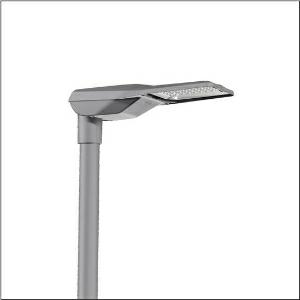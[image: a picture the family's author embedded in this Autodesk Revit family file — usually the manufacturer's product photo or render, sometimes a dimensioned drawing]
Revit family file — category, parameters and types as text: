
# Revit family: streetlight_sl_21_iq_mini___st0_8a_5xe2c41d08jb_a90a
name_source: partatom
category: Lighting Fixtures
units: mm (PartAtom-declared; Revit-internal decimal feet)

## family parameters
Cut with Voids When Loaded = No
Host = Face
Light Source = No
Part Type = Normal
Room Calculation Point = No
Round Connector Dimension = Use Diameter
Shared = No

## types (1)
- --- (1 x LED, 11290 lm, 71.6 W, 4000K)
    Apparent Load = 72 VA
    CIE Flux Codes = 41 75 97 100 100
    Color Rendering = 70
    Color Temperature = 4000K
    Default Elevation = 1800 mm
    Description = Streetlight SL 21 iQ mini, mast luminaire, primary light control with lens, of PMMA, primary optical cover: cover, of toughened safety glass, transparent, light distribution: ST0.8a, light emission: direct distribution, primary light characteristic: asymmetric, installation type: post-top, side-entry, LED, High Power LED, rated luminous flux: 11.290lm, luminous efficacy: 158lm/W, light colour: 740, colour temperature: 4000K, control gear: iQ-Comfort, control: Auto-Match, Temp-Guard, Lumen-Switch, Night-Set, Smart-Wire, Light-Fading, Desk-Remote (wireless, voltage-free reading and setting of iQ features in the workshop via application-optimized NFC function/RFID function), optimised constant luminous flux control (CLO 2.0), pre-setting: linear dimming characteristic, mains connection: 220..240V, AC, 50/60Hz, start of lifetime: 72W, end of service life: 75W, reduction: 33W, luminaire housing, of diecast aluminium, powder-coated, Siteco® metallic grey (DB 702S), corrosivity category C5 mid according to DIN EN ISO 12944, please order mast flange separately, inclination adjustable: 0°, 5°, 10°, 15°, sealing non-destructively replaceable, multi-level sealing system, length: 628mm, width: 235mm, height: 110mm, mast flange for spigot size: 42mm (side-entry): 5XC10008XM4, 60/48mm (side-entry/post-top): 5XC10108XM2, 76/60mm (side-entry/post-top): 5XC10108XM1, mounting height: 4..8m, protection rating (complete): IP66, insulation class (complete): insulation class II (safety insulation), certification: CE, ENEC, ENEC+, VDE, impact resistance: IK10, permissible operating ambient temperature for outdoor applications: -40..+50°C, standard-compliant lighting for roads and squares, packaging unit: 1 piece

Light Distribution: ST0.8a
    Height = 110 mm
    Lamp = 1 x LED
    Lamp Light Flux = 11290 lm
    Lamp Power = 71.6 W
    Lamp count = 1
    Length = 625 mm
    Luminous efficacy = 158 lm/W
    Manufacturer = Siteco
    ModVariant = No
    Model = 5XE2C41D08JB
    Number of Poles = 1
    OnlyDefault = Yes
    Power Factor = 1
    Product Name = Streetlight SL 21 iQ mini | ST0.8a
    Product group = mast luminaire | pylon top
    ProductGroupID = 6100
    Protection Class = Protection class II
    Protection Degree = IP 66
    RLX_Detail_Level = 1
    RLX_Emergency_Light_Flux = 0 lm
    RLX_Emergency_Type = 0
    RLX_Emergency_Type_DB = No
    RlxData = <blob elided: 26361 chars, md5=cf60f9b4>
    Socket = socket
    Standby Power = 0 W
    System Light Flux = 11290 lm
    System Power = 72 W
    Type Comments = factory setting: luminous flux: 100 % | dim-lin: 254 | 746 mA
    Type Image = l_1003519.jpg
    URL = http://relux.com
    VarID = @adj_169230
    Voltage = 0 V
    Weight = 0.00 kg
    Width = 234 mm

## geometry (parser evidence)
native form markers: Blend x4, Sweep x11
no freeform markers — native parametric forms only
